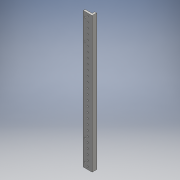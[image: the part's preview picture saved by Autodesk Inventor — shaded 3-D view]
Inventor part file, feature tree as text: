
AUTODESK INVENTOR PART (.ipt)
format: ipt  version: 2016 (Build 200138000, 138)  size: 145,920 bytes
history: native  units: mm
features: reference x31, extrude x2, sketch x2
ambient origin geometry x8: Origin, YZ Plane, XZ Plane, XY Plane, X Axis, Y Axis, Z Axis, Center Point
bodies: Body1 (feature_tree)
feature tree (35):
  extrude  "Extrusion4"  Depth=416.0mm
  extrude  "Extrusion5"  Depth=8.0mm
  sketch  "Sketch1"  dims[d0=27.0mm d1=416.0mm]
  reference  "Reference1"
  reference  "Reference2"
  reference  "Reference3"
  reference  "Reference4"
  reference  "Reference5"
  reference  "Reference6"
  reference  "Reference7"
  reference  "Reference8"
  reference  "Reference9"
  reference  "Reference10"
  reference  "Reference11"
  reference  "Reference12"
  reference  "Reference15"
  reference  "Reference16"
  reference  "Reference17"
  reference  "Reference18"
  reference  "Reference19"
  reference  "Reference20"
  reference  "Reference21"
  reference  "Reference22"
  reference  "Reference23"
  reference  "Reference24"
  reference  "Reference25"
  reference  "Reference26"
  reference  "Reference27"
  reference  "Reference28"
  reference  "Reference29"
  reference  "Reference31"
  reference  "Reference32"
  reference  "Reference35"
  reference  "Reference37"
  sketch  "Sketch2"  dims[d8=6.0mm d9=0.0mm d10=3.0mm d11=6.0mm d12=8.0mm d13=0.0mm]
